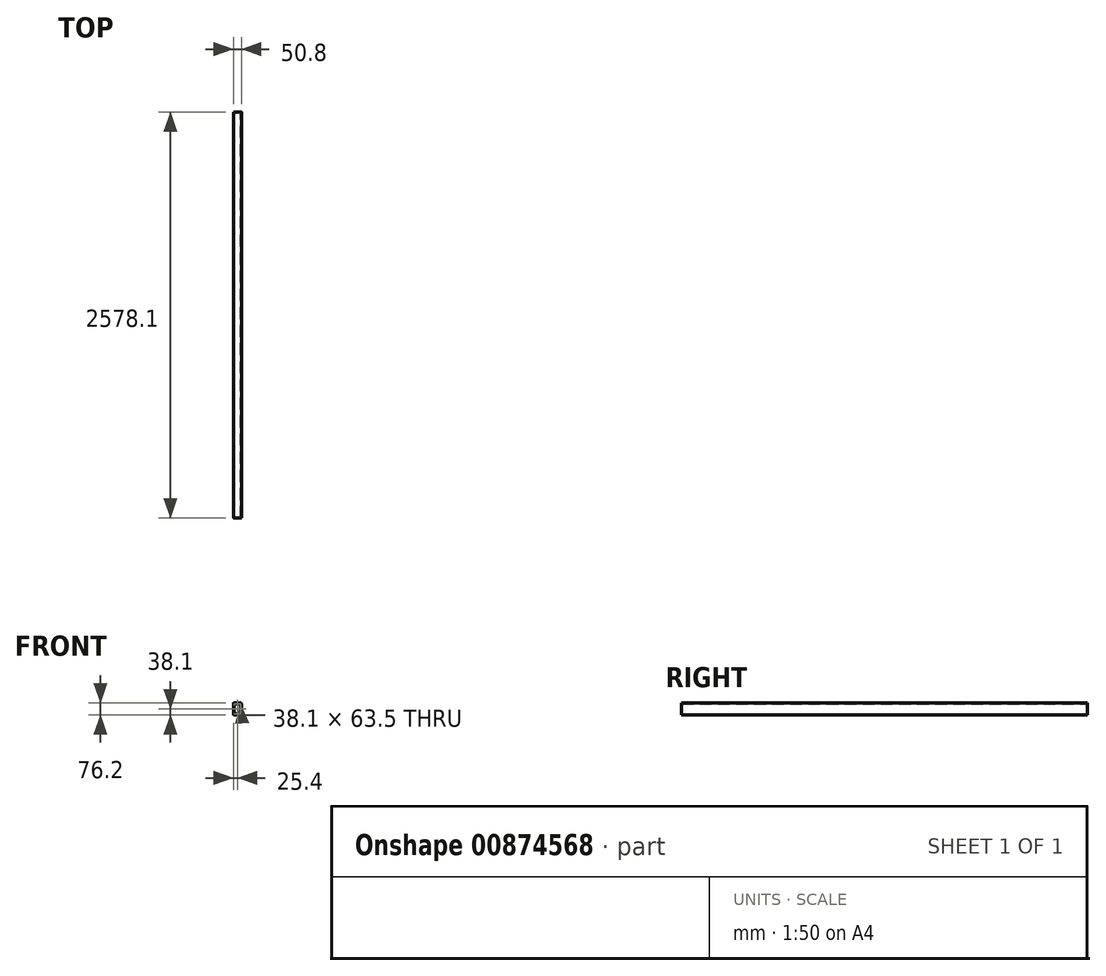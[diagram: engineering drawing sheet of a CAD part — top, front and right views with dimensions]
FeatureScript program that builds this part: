
annotation { "Feature Type Name" : "Feature", "Feature Type Description" : "" }
export const myFeature = defineFeature(function(context is Context, id is Id, definition is map)
    precondition{}
    {
        {
            var Q0;
            Q0=qCreatedBy(makeId("Front.planeOp"),FACE);
            var sketch = newSketch(context, id + "F0", { "sketchPlane" : qUnion([Q0])});
            skLineSegment(sketch, "E0.bottom", {"start": v(-19.05, 38.1) * mm, "end": v(19.05, 38.1) * mm});
            skLineSegment(sketch, "E0.top", {"start": v(-19.05, -38.1) * mm, "end": v(19.05, -38.1) * mm});
            skLineSegment(sketch, "E0.left", {"start": v(-25.4, 31.75) * mm, "end": v(-25.4, -31.75) * mm});
            skLineSegment(sketch, "E0.right", {"start": v(25.4, 31.75) * mm, "end": v(25.4, -31.75) * mm});
            skPoint(sketch, "E0.middle", {"position": v(0, 0) * mm});
            skLineSegment(sketch, "E1.bottom", {"start": v(-19.05, 31.75) * mm, "end": v(19.05, 31.75) * mm});
            skLineSegment(sketch, "E1.top", {"start": v(-19.05, -31.75) * mm, "end": v(19.05, -31.75) * mm});
            skLineSegment(sketch, "E1.left", {"start": v(-19.05, 31.75) * mm, "end": v(-19.05, -31.75) * mm});
            skLineSegment(sketch, "E1.right", {"start": v(19.05, 31.75) * mm, "end": v(19.05, -31.75) * mm});
            skPoint(sketch, "E2.visualSharp", {"position": v(-25.4, 38.1) * mm});
            skArc(sketch, "E2.filletArc", {"start": v(-19.05, 38.1) * mm, "mid": v(-23.54, 36.24) * mm, "end": v(-25.4, 31.75) * mm});
            skPoint(sketch, "E3.visualSharp", {"position": v(25.4, 38.1) * mm});
            skArc(sketch, "E3.filletArc", {"start": v(25.4, 31.75) * mm, "mid": v(23.54, 36.24) * mm, "end": v(19.05, 38.1) * mm});
            skPoint(sketch, "E4.visualSharp", {"position": v(25.4, -38.1) * mm});
            skArc(sketch, "E4.filletArc", {"start": v(19.05, -38.1) * mm, "mid": v(23.54, -36.24) * mm, "end": v(25.4, -31.75) * mm});
            skPoint(sketch, "E5.visualSharp", {"position": v(-25.4, -38.1) * mm});
            skArc(sketch, "E5.filletArc", {"start": v(-25.4, -31.75) * mm, "mid": v(-23.54, -36.24) * mm, "end": v(-19.05, -38.1) * mm});
            skSolve(sketch);
        }
        {
            var Q0;
            Q0=makeQuery(id+"F0.imprint","IMPRINT",FACE,{"disambiguationData":[TD([[makeQuery(id+"F0.imprint","IMPRINT",EDGE,{"derivedFrom":sQuery(id+"F0.wireOp",EDGE,"E0.bottom")}),-1.0]])]});
            extrude(context, id + "F1", {"entities" : qUnion([Q0]), "depth" : 2578.1 * mm, "offsetDistance" : 25.4 * mm});
        }
    });
